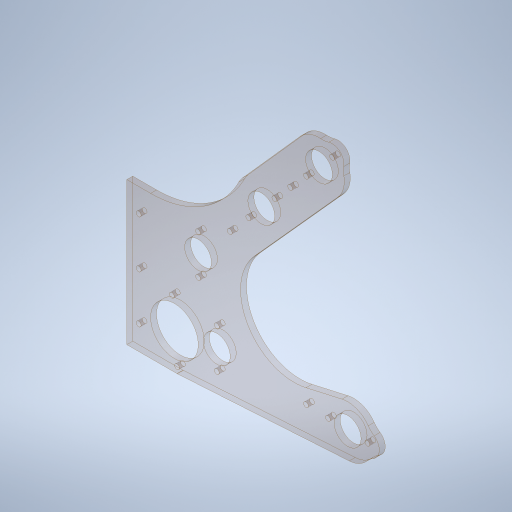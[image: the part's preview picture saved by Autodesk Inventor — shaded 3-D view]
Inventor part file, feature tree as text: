
AUTODESK INVENTOR PART (.ipt)
format: ipt  version: 2023.4 (Build 274418000, 418)  size: 387,584 bytes
history: native  units: in
note: dims shown in document units (in); Inventor stores cm internally (conversion verified against a paired STEP export)
features: sketch x2, extrude x1, hole x1, fillet x1
ambient origin geometry x8: Origin, YZ Plane, XZ Plane, XY Plane, X Axis, Y Axis, Z Axis, Center Point
bodies: Body1 (feature_tree)
feature tree (5):
  sketch  "Sketch1"  dims[d0=4.0in d2=3.0in]
  sketch  "Sketch4"  dims[d3=3.0in d4=3.0in d8=16.0in d9=12.0in d11=12.0in d13=4.5in d14=4.25in d15=0.5in d16=3.642in d17=60.0deg d63=1.125in d64=3.125in d65=1.88in d66=5.499in d67=4.018in d68=0.4688in d69=2.0in d70=0.5in d71=0.0172in d72=0.5841in d73=1.0in d74=6.0in d75=4.0in d76=1.655in d77=0.5in d79=1.0in d80=0.75in d81=1.375in d82=0.25in d83=0.0in d84=0.201in d85=0.75in d86=0.375in d87=0.25in d88=0.5635in d89=1.0in d90=0.8108in d91=1.0in d92=0.5in d93=2.3622in d95=360.0deg]
  extrude  "Extrusion2"  Depth=3.0in
  hole  "Hole2"  [1 undecoded]
  fillet  "Fillet2"  Radius=16.0in
note: 1 required parameter value undecoded (feature->parameter linkage not recoverable at this tier; creation-order binding heuristic only, values carry confidence <= 0.55)
